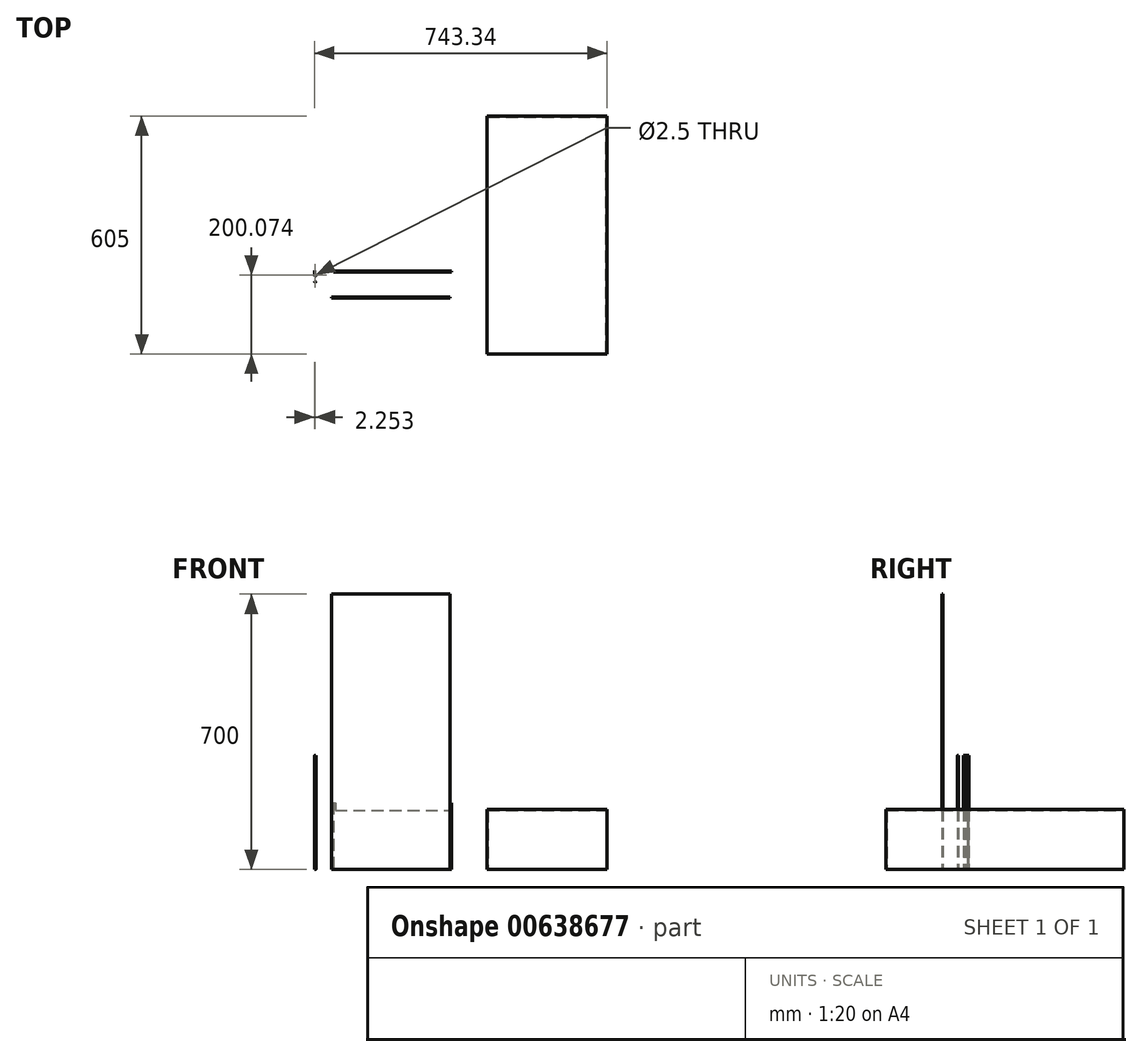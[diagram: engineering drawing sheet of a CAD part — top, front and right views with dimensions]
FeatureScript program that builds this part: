
annotation { "Feature Type Name" : "Feature", "Feature Type Description" : "" }
export const myFeature = defineFeature(function(context is Context, id is Id, definition is map)
    precondition{}
    {
        {
            var Q0;
            Q0=qCreatedBy(makeId("Top.planeOp"),FACE);
            var sketch = newSketch(context, id + "F0", { "sketchPlane" : qUnion([Q0])});
            skLineSegment(sketch, "E0.bottom", {"start": v(-15.55, 46.39) * mm, "end": v(284.45, 46.39) * mm});
            skLineSegment(sketch, "E0.top", {"start": v(-15.55, 43.89) * mm, "end": v(284.45, 43.89) * mm});
            skLineSegment(sketch, "E0.left", {"start": v(-15.55, 46.39) * mm, "end": v(-15.55, 43.89) * mm});
            skLineSegment(sketch, "E0.right", {"start": v(284.45, 46.39) * mm, "end": v(284.45, 43.89) * mm});
            skCircle(sketch, "E1", {"center": v(-61.57, 19.28) * mm, "radius": 1.25 * mm});
            skCircle(sketch, "E2", {"center": v(-61.57, 36.05) * mm, "radius": 1.25 * mm});
            skCircle(sketch, "E3", {"center": v(-61.57, 36.05) * mm, "radius": 2.25 * mm});
            skLineSegment(sketch, "E4", {"start": v(-63.82, 36.05) * mm, "end": v(-63.82, 47.93) * mm});
            skLineSegment(sketch, "E5", {"start": v(-63.82, 47.93) * mm, "end": v(-62.82, 47.93) * mm});
            skLineSegment(sketch, "E6", {"start": v(-62.82, 47.93) * mm, "end": v(-62.82, 37.93) * mm});
            skLineSegment(sketch, "E7.bottom", {"start": v(-19.6, -19.1) * mm, "end": v(280.4, -19.1) * mm});
            skLineSegment(sketch, "E7.top", {"start": v(-19.6, -21.6) * mm, "end": v(280.4, -21.6) * mm});
            skLineSegment(sketch, "E7.left", {"start": v(-19.6, -19.1) * mm, "end": v(-19.6, -21.6) * mm});
            skLineSegment(sketch, "E7.right", {"start": v(280.4, -19.1) * mm, "end": v(280.4, -21.6) * mm});
            skLineSegment(sketch, "E8.bottom", {"start": v(374.52, -164.02) * mm, "end": v(679.52, -164.02) * mm});
            skLineSegment(sketch, "E8.top", {"start": v(374.52, 440.98) * mm, "end": v(679.52, 440.98) * mm});
            skLineSegment(sketch, "E8.left", {"start": v(374.52, -164.02) * mm, "end": v(374.52, 440.98) * mm});
            skLineSegment(sketch, "E8.right", {"start": v(679.52, -164.02) * mm, "end": v(679.52, 440.98) * mm});
            skSolve(sketch);
        }
        {
            var Q0;
            Q0=makeQuery(id+"F0.imprint","IMPRINT",FACE,{"disambiguationData":[TD([[makeQuery(id+"F0.imprint","IMPRINT",EDGE,{"derivedFrom":sQuery(id+"F0.wireOp",EDGE,"E0.bottom")}),-1.0]])]});
            extrude(context, id + "F1", {"entities" : qUnion([Q0]), "depth" : 170 * mm, "offsetDistance" : 25 * mm});
        }
        {
            var Q0;
            Q0=makeQuery(id+"F1.opExtrude","SWEPT_FACE",FACE,{"disambiguationData":[OSD([sQuery(id+"F0.wireOp",EDGE,"E0.top")])]});
            var sketch = newSketch(context, id + "F2", { "sketchPlane" : qUnion([Q0])});
            skLineSegment(sketch, "E9", {"start": v(-10.55, 170) * mm, "end": v(-10.55, 150) * mm});
            skLineSegment(sketch, "E10", {"start": v(-10.55, 150) * mm, "end": v(279.45, 150) * mm});
            skLineSegment(sketch, "E11", {"start": v(279.45, 150) * mm, "end": v(279.45, 170) * mm});
            skLineSegment(sketch, "E12", {"start": v(-15.55, 10) * mm, "end": v(284.45, 10) * mm});
            skSolve(sketch);
        }
        {
            var Q0;
            {var subQ0=sQuery(id+"F2.wireOp",EDGE,"E9");Q0=makeQuery(id+"F2.imprint","IMPRINT",FACE,{"disambiguationData":[TD([[makeQuery(id+"F2.imprint","IMPRINT",EDGE,{"derivedFrom":subQ0}),1.0]])]});}
            extrude(context, id + "F3", {"entities" : qUnion([Q0]), "operationType" : NewBodyOperationType.REMOVE, "oppositeDirection" : true, "depth" : 25 * mm, "offsetDistance" : 25 * mm});
        }
        {
            var Q0;
            Q0=makeQuery(id+"F0.imprint","IMPRINT",FACE,{"disambiguationData":[TD([[makeQuery(id+"F0.imprint","IMPRINT",EDGE,{"derivedFrom":sQuery(id+"F0.wireOp",EDGE,"E1")}),1.0]])]});
            extrude(context, id + "F4", {"entities" : qUnion([Q0]), "depth" : 290 * mm, "offsetDistance" : 25 * mm});
        }
        {
            var Q0;
            Q0=makeQuery(id+"F0.imprint","IMPRINT",FACE,{"disambiguationData":[TD([[makeQuery(id+"F0.imprint","IMPRINT",EDGE,{"derivedFrom":sQuery(id+"F0.wireOp",EDGE,"E2")}),-1.0]])]});
            var Q1;
            {var subQ0=sQuery(id+"F0.wireOp",EDGE,"E4");Q1=makeQuery(id+"F0.imprint","IMPRINT",FACE,{"disambiguationData":[TD([[makeQuery(id+"F0.imprint","IMPRINT",EDGE,{"derivedFrom":subQ0}),-1.0]])]});}
            extrude(context, id + "F5", {"entities" : qUnion([Q0, Q1]), "depth" : 290 * mm, "offsetDistance" : 25 * mm});
        }
        {
            var Q0;
            Q0=makeQuery(id+"F0.imprint","IMPRINT",FACE,{"disambiguationData":[TD([[makeQuery(id+"F0.imprint","IMPRINT",EDGE,{"derivedFrom":sQuery(id+"F0.wireOp",EDGE,"E7.bottom")}),-1.0]])]});
            extrude(context, id + "F6", {"entities" : qUnion([Q0]), "depth" : 700 * mm, "offsetDistance" : 25 * mm});
        }
        {
            var Q0;
            Q0=makeQuery(id+"F6.opExtrude","SWEPT_FACE",FACE,{"disambiguationData":[OSD([sQuery(id+"F0.wireOp",EDGE,"E7.bottom")])]});
            var sketch = newSketch(context, id + "F7", { "sketchPlane" : qUnion([Q0])});
            skLineSegment(sketch, "E13", {"start": v(19.6, 10) * mm, "end": v(-280.4, 10) * mm});
            skSolve(sketch);
        }
        {
            var Q0;
            Q0=makeQuery(id+"F5.opExtrude","SWEPT_FACE",FACE,{"disambiguationData":[OSD([sQuery(id+"F0.wireOp",EDGE,"E4")])]});
            var sketch = newSketch(context, id + "F8", { "sketchPlane" : qUnion([Q0])});
            skLineSegment(sketch, "E14", {"start": v(-37.93, 290) * mm, "end": v(-37.93, 0) * mm});
            skSolve(sketch);
        }
        {
            var Q0;
            Q0=makeQuery(id+"F0.imprint","IMPRINT",FACE,{"disambiguationData":[TD([[makeQuery(id+"F0.imprint","IMPRINT",EDGE,{"derivedFrom":sQuery(id+"F0.wireOp",EDGE,"E8.bottom")}),1.0]])]});
            extrude(context, id + "F9", {"entities" : qUnion([Q0]), "depth" : 152.5 * mm, "offsetDistance" : 25 * mm});
        }
        {
            var Q0;
            Q0=makeQuery(id+"F9.opExtrude","CAP_FACE",FACE,{"disambiguationData":[OSD([sQuery(id+"F0.wireOp",EDGE,"E8.bottom"),sQuery(id+"F0.wireOp",EDGE,"E8.top"),sQuery(id+"F0.wireOp",EDGE,"E8.left"),sQuery(id+"F0.wireOp",EDGE,"E8.right")])],"isStart":true});
            shell(context, id + "F10", {"entities" : qUnion([Q0]), "thickness" : 2.5 * mm});
        }
        {
            var Q0;
            Q0=makeQuery(id+"F9.opExtrude","SWEPT_FACE",FACE,{"disambiguationData":[OSD([sQuery(id+"F0.wireOp",EDGE,"E8.bottom")])]});
            var sketch = newSketch(context, id + "F11", { "sketchPlane" : qUnion([Q0])});
            skLineSegment(sketch, "E15", {"start": v(679.52, 142.5) * mm, "end": v(374.52, 142.5) * mm});
            skSolve(sketch);
        }
    });
